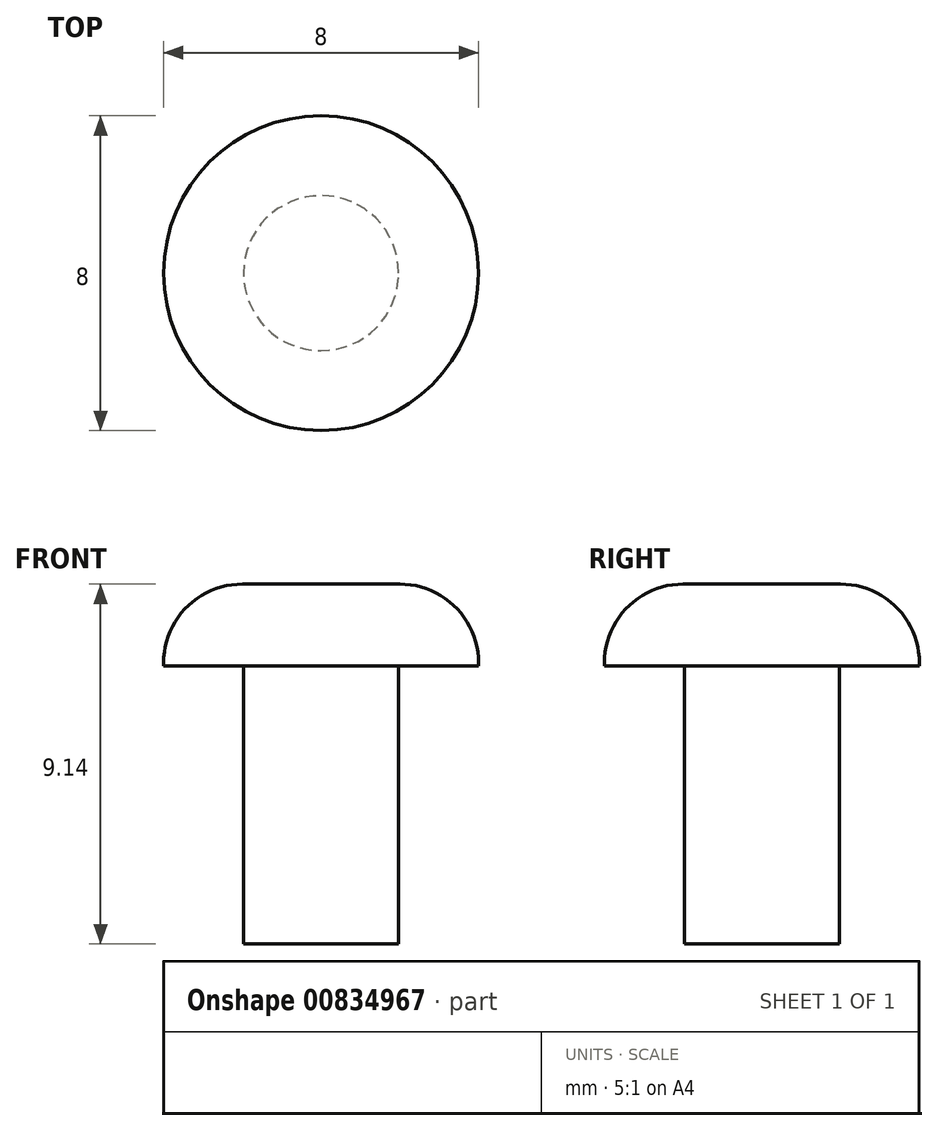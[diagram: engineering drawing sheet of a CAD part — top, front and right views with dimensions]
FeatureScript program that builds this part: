
annotation { "Feature Type Name" : "Feature", "Feature Type Description" : "" }
export const myFeature = defineFeature(function(context is Context, id is Id, definition is map)
    precondition{}
    {
        {
            var Q0;
            Q0=qCreatedBy(makeId("Front.planeOp"),FACE);
            var sketch = newSketch(context, id + "F0", { "sketchPlane" : qUnion([Q0])});
            skLineSegment(sketch, "E0", {"start": v(-1.97, 0) * mm, "end": v(-1.97, 7.06) * mm});
            skLineSegment(sketch, "E1", {"start": v(-1.97, 7.06) * mm, "end": v(-4, 7.06) * mm});
            skLineSegment(sketch, "E2", {"start": v(-4, 7.06) * mm, "end": v(-4, 7.14) * mm});
            skLineSegment(sketch, "E3", {"start": v(-2, 9.14) * mm, "end": v(0, 9.14) * mm});
            skLineSegment(sketch, "E4", {"start": v(0, 9.14) * mm, "end": v(0, 0) * mm});
            skLineSegment(sketch, "E5", {"start": v(0, 0) * mm, "end": v(-1.97, 0) * mm});
            skPoint(sketch, "E6.visualSharp", {"position": v(-4, 9.14) * mm});
            skArc(sketch, "E6.filletArc", {"start": v(-2, 9.14) * mm, "mid": v(-3.41, 8.55) * mm, "end": v(-4, 7.14) * mm});
            skSolve(sketch);
        }
        {
            var Q0;
            Q0 = qSketchRegion(id + "F0", true);
            var Q1;
            Q1=sQuery(id+"F0.wireOp",EDGE,"E4");
            revolve(context, id + "F1", {"surfaceOperationType" : NewSurfaceOperationType.NEW, "entities" : qUnion([Q0]), "axis" : qUnion([Q1]), "revolveType" : RevolveType.FULL});
        }
    });
